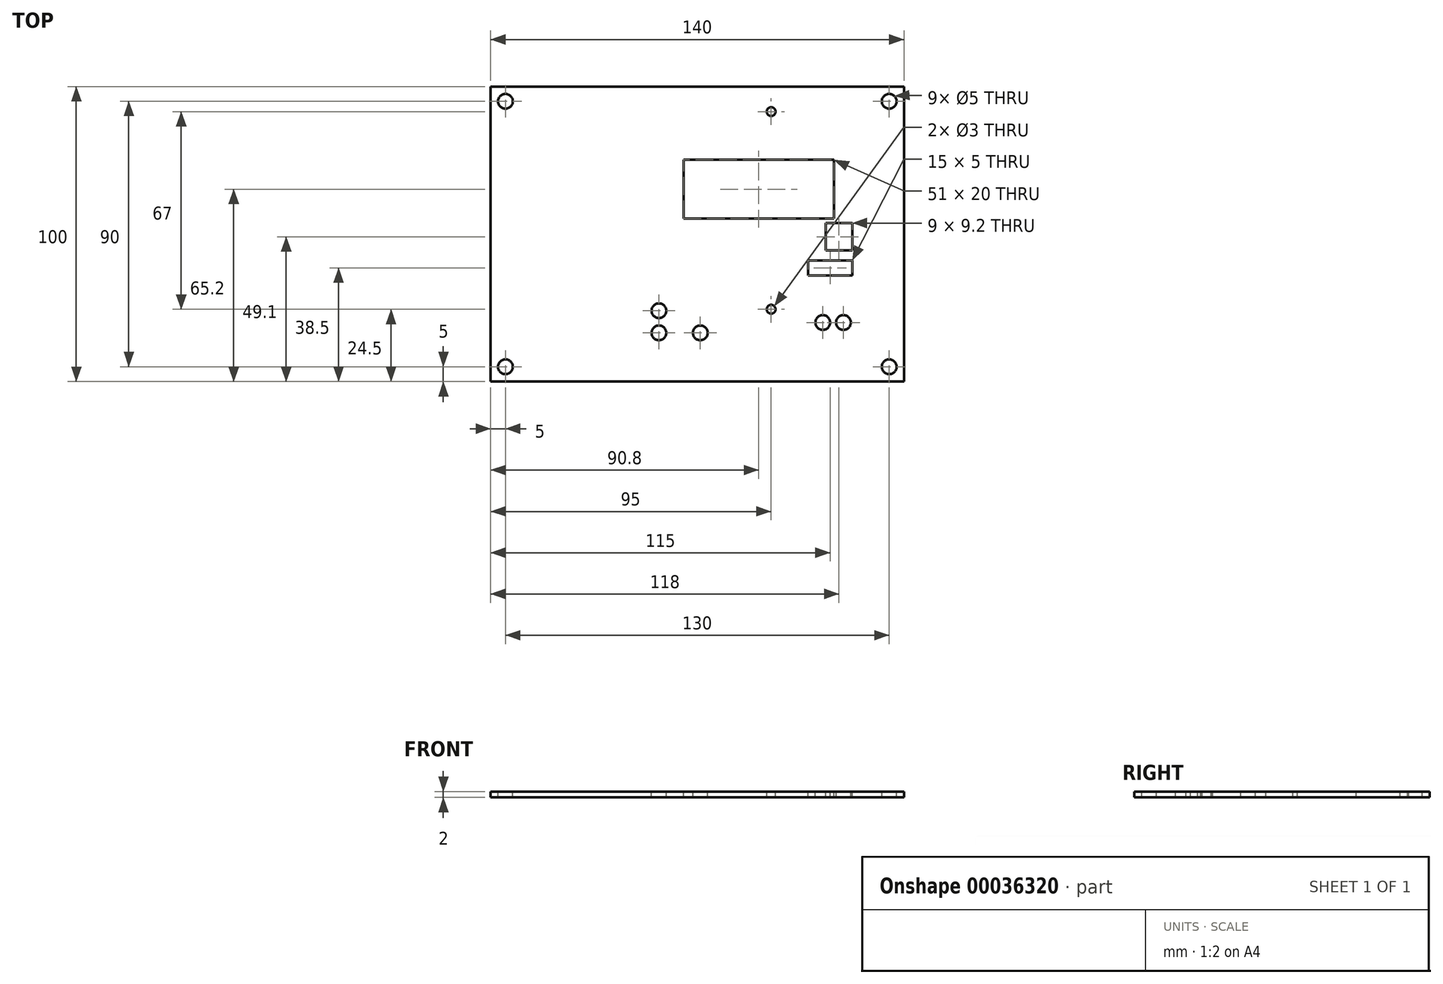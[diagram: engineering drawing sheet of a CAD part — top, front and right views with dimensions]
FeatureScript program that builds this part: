
annotation { "Feature Type Name" : "Feature", "Feature Type Description" : "" }
export const myFeature = defineFeature(function(context is Context, id is Id, definition is map)
    precondition{}
    {
        {
            var Q0;
            Q0=qCreatedBy(makeId("Top.planeOp"),FACE);
            var sketch = newSketch(context, id + "F0", { "sketchPlane" : qUnion([Q0])});
            skLineSegment(sketch, "E0.bottom", {"start": v(-70, 50) * mm, "end": v(70, 50) * mm});
            skLineSegment(sketch, "E0.top", {"start": v(-70, -50) * mm, "end": v(70, -50) * mm});
            skLineSegment(sketch, "E0.left", {"start": v(-70, 50) * mm, "end": v(-70, -50) * mm});
            skLineSegment(sketch, "E0.right", {"start": v(70, 50) * mm, "end": v(70, -50) * mm});
            skLineSegment(sketch, "E1", {"start": v(-70, 0) * mm, "end": v(70, 0) * mm, "construction": true});
            skLineSegment(sketch, "E2.bottom", {"start": v(-52.5, 3.7) * mm, "end": v(-43.5, 3.7) * mm});
            skLineSegment(sketch, "E2.top", {"start": v(-52.5, -5.5) * mm, "end": v(-43.5, -5.5) * mm});
            skLineSegment(sketch, "E2.left", {"start": v(-52.5, 3.7) * mm, "end": v(-52.5, -5.5) * mm});
            skLineSegment(sketch, "E2.right", {"start": v(-43.5, 3.7) * mm, "end": v(-43.5, -5.5) * mm});
            skLineSegment(sketch, "E3.bottom", {"start": v(-46.3, 25.2) * mm, "end": v(4.7, 25.2) * mm});
            skLineSegment(sketch, "E3.top", {"start": v(-46.3, 5.2) * mm, "end": v(4.7, 5.2) * mm});
            skLineSegment(sketch, "E3.left", {"start": v(-46.3, 25.2) * mm, "end": v(-46.3, 5.2) * mm});
            skLineSegment(sketch, "E3.right", {"start": v(4.7, 25.2) * mm, "end": v(4.7, 5.2) * mm});
            skCircle(sketch, "E4", {"center": v(-1, -33.5) * mm, "radius": 2.5 * mm});
            skCircle(sketch, "E5", {"center": v(13, -26) * mm, "radius": 2.5 * mm});
            skCircle(sketch, "E6", {"center": v(13, -33.5) * mm, "radius": 2.5 * mm});
            skCircle(sketch, "E7", {"center": v(-25, -25.5) * mm, "radius": 1.5 * mm});
            skCircle(sketch, "E8", {"center": v(-49.5, -30) * mm, "radius": 2.5 * mm});
            skCircle(sketch, "E9", {"center": v(-42.5, -30) * mm, "radius": 2.5 * mm});
            skLineSegment(sketch, "E10.bottom", {"start": v(-60, 41.5) * mm, "end": v(35, 41.5) * mm, "construction": true});
            skLineSegment(sketch, "E10.top", {"start": v(-60, -41.5) * mm, "end": v(35, -41.5) * mm, "construction": true});
            skLineSegment(sketch, "E10.left", {"start": v(-60, 41.5) * mm, "end": v(-60, -41.5) * mm, "construction": true});
            skLineSegment(sketch, "E10.right", {"start": v(35, 41.5) * mm, "end": v(35, -41.5) * mm, "construction": true});
            skLineSegment(sketch, "E11", {"start": v(-33.16, 50) * mm, "end": v(-33.16, 41.5) * mm, "construction": true});
            skLineSegment(sketch, "E12", {"start": v(-33.52, -41.5) * mm, "end": v(-33.52, -50) * mm, "construction": true});
            skLineSegment(sketch, "E13", {"start": v(-46.3, 15.2) * mm, "end": v(-60, 15.2) * mm, "construction": true});
            skLineSegment(sketch, "E14", {"start": v(-20.02, 25.2) * mm, "end": v(-20.02, 50) * mm, "construction": true});
            skLineSegment(sketch, "E15", {"start": v(-52.5, -0.9) * mm, "end": v(-60, -0.9) * mm, "construction": true});
            skLineSegment(sketch, "E16", {"start": v(-49.48, 3.7) * mm, "end": v(-49.48, 41.5) * mm, "construction": true});
            skLineSegment(sketch, "E17", {"start": v(-49.5, -30) * mm, "end": v(-49.5, -41.5) * mm, "construction": true});
            skLineSegment(sketch, "E18", {"start": v(-42.5, -30) * mm, "end": v(-49.5, -30) * mm, "construction": true});
            skLineSegment(sketch, "E19.bottom", {"start": v(-52.5, -9) * mm, "end": v(-37.5, -9) * mm});
            skLineSegment(sketch, "E19.top", {"start": v(-52.5, -14) * mm, "end": v(-37.5, -14) * mm});
            skLineSegment(sketch, "E19.left", {"start": v(-52.5, -9) * mm, "end": v(-52.5, -14) * mm});
            skLineSegment(sketch, "E19.right", {"start": v(-37.5, -9) * mm, "end": v(-37.5, -14) * mm});
            skLineSegment(sketch, "E20", {"start": v(-37.5, -11.5) * mm, "end": v(-52.5, -11.5) * mm, "construction": true});
            skCircle(sketch, "E21", {"center": v(-25, 41.5) * mm, "radius": 1.5 * mm});
            skCircle(sketch, "E22", {"center": v(-65, 45) * mm, "radius": 2.5 * mm});
            skCircle(sketch, "E23", {"center": v(-65, -45) * mm, "radius": 2.5 * mm});
            skCircle(sketch, "E24", {"center": v(65, -45) * mm, "radius": 2.5 * mm});
            skCircle(sketch, "E25", {"center": v(65, 45) * mm, "radius": 2.5 * mm});
            skSolve(sketch);
        }
        {
            var Q0;
            Q0=makeQuery(id+"F0.imprint","IMPRINT",FACE,{"disambiguationData":[TD([[makeQuery(id+"F0.imprint","IMPRINT",EDGE,{"derivedFrom":sQuery(id+"F0.wireOp",EDGE,"E0.bottom")}),-1.0]])]});
            extrude(context, id + "F1", {"entities" : qUnion([Q0]), "depth" : 2 * mm});
        }
        {
            var Q0;
            Q0=makeQuery(id+"F1.opExtrude","SWEPT_BODY",BODY,{"disambiguationData":[OSD([sQuery(id+"F0.wireOp",EDGE,"E0.bottom"),sQuery(id+"F0.wireOp",EDGE,"E0.top"),sQuery(id+"F0.wireOp",EDGE,"E0.left"),sQuery(id+"F0.wireOp",EDGE,"E0.right"),sQuery(id+"F0.wireOp",EDGE,"E2.bottom"),sQuery(id+"F0.wireOp",EDGE,"E2.top"),sQuery(id+"F0.wireOp",EDGE,"E2.left"),sQuery(id+"F0.wireOp",EDGE,"E2.right"),sQuery(id+"F0.wireOp",EDGE,"E3.bottom"),sQuery(id+"F0.wireOp",EDGE,"E3.top"),sQuery(id+"F0.wireOp",EDGE,"E3.left"),sQuery(id+"F0.wireOp",EDGE,"E3.right"),sQuery(id+"F0.wireOp",EDGE,"E4"),sQuery(id+"F0.wireOp",EDGE,"E5"),sQuery(id+"F0.wireOp",EDGE,"E6"),sQuery(id+"F0.wireOp",EDGE,"E7"),sQuery(id+"F0.wireOp",EDGE,"E8"),sQuery(id+"F0.wireOp",EDGE,"E9"),sQuery(id+"F0.wireOp",EDGE,"E19.bottom"),sQuery(id+"F0.wireOp",EDGE,"E19.top"),sQuery(id+"F0.wireOp",EDGE,"E19.left"),sQuery(id+"F0.wireOp",EDGE,"E19.right"),sQuery(id+"F0.wireOp",EDGE,"E21"),sQuery(id+"F0.wireOp",EDGE,"E22"),sQuery(id+"F0.wireOp",EDGE,"E23"),sQuery(id+"F0.wireOp",EDGE,"E24"),sQuery(id+"F0.wireOp",EDGE,"E25")])]});
            var Q1;
            Q1=makeQuery(id+"F1.opExtrude","CAP_EDGE",EDGE,{"disambiguationData":[OSD([sQuery(id+"F0.wireOp",EDGE,"E0.left")])],"isStart":false});
            transform(context, id + "F2", {"entities" : qUnion([Q0]), "transformType" : TransformType.ROTATION, "transformAxis" : qUnion([Q1]), "angle" : 180 * degree, "makeCopy" : false});
        }
    });
